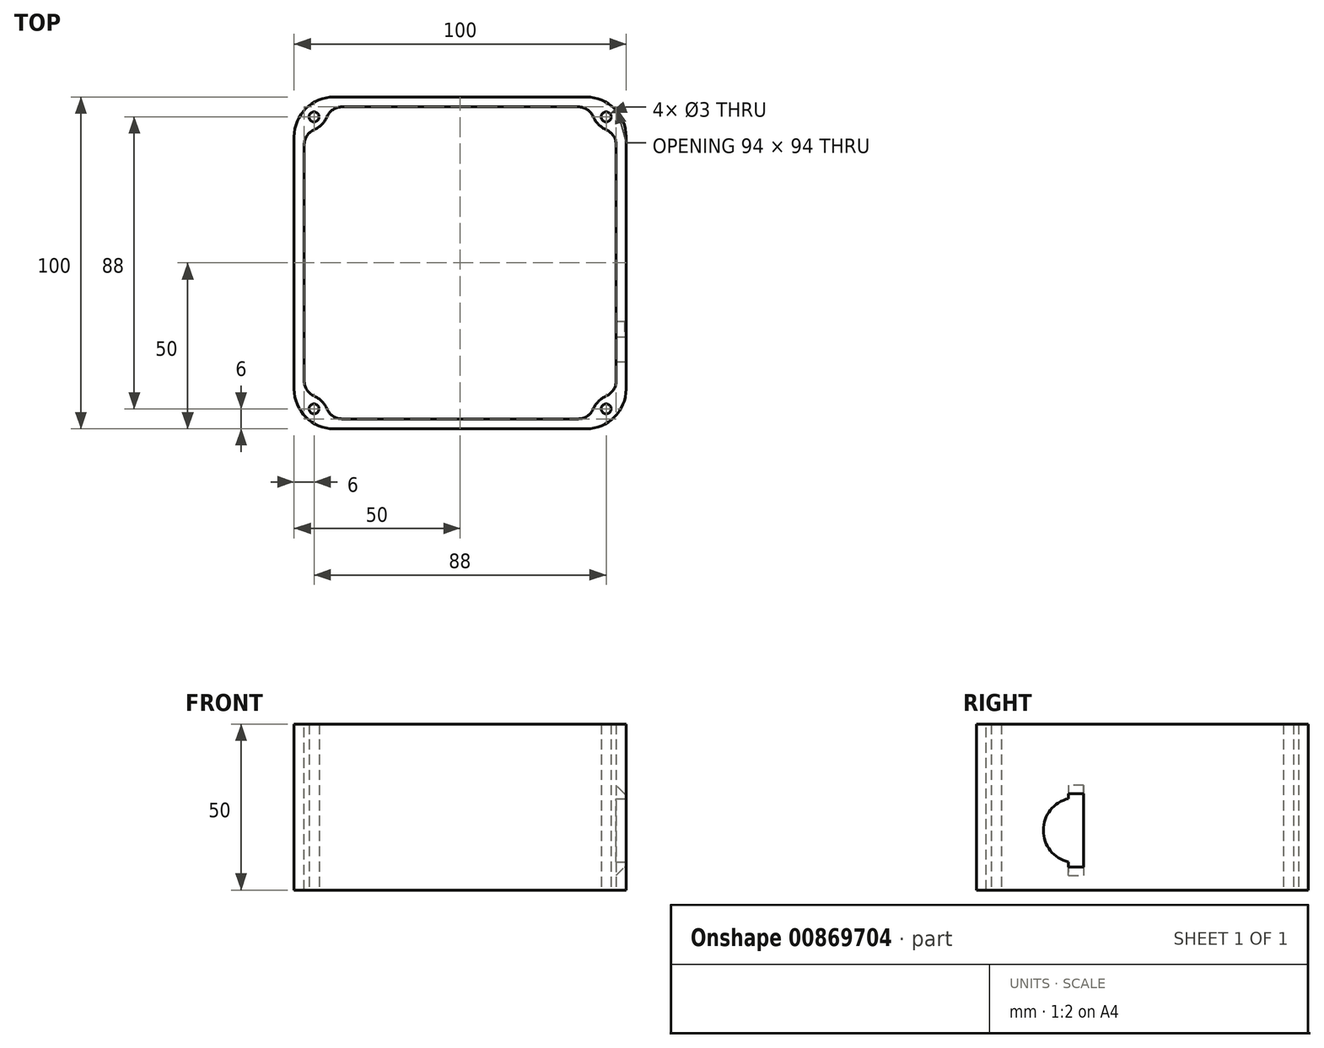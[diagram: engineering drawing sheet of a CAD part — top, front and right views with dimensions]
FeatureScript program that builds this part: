
annotation { "Feature Type Name" : "Feature", "Feature Type Description" : "" }
export const myFeature = defineFeature(function(context is Context, id is Id, definition is map)
    precondition{}
    {
        {
            var Q0;
            Q0=qCreatedBy(makeId("Top.planeOp"),FACE);
            var sketch = newSketch(context, id + "F0", { "sketchPlane" : qUnion([Q0])});
            skLineSegment(sketch, "E0.bottom", {"start": v(50, -50) * mm, "end": v(-50, -50) * mm});
            skLineSegment(sketch, "E0.top", {"start": v(50, 50) * mm, "end": v(-50, 50) * mm});
            skLineSegment(sketch, "E0.left", {"start": v(50, -50) * mm, "end": v(50, 50) * mm});
            skLineSegment(sketch, "E0.right", {"start": v(-50, -50) * mm, "end": v(-50, 50) * mm});
            skPoint(sketch, "E0.middle", {"position": v(0, 0) * mm});
            skLineSegment(sketch, "E1.bottom", {"start": v(47, -47) * mm, "end": v(-47, -47) * mm});
            skLineSegment(sketch, "E1.top", {"start": v(47, 47) * mm, "end": v(-47, 47) * mm});
            skLineSegment(sketch, "E1.left", {"start": v(47, -47) * mm, "end": v(47, 47) * mm});
            skLineSegment(sketch, "E1.right", {"start": v(-47, -47) * mm, "end": v(-47, 47) * mm});
            skLineSegment(sketch, "E2.bottom", {"start": v(-47, 47) * mm, "end": v(-44, 47) * mm, "construction": true});
            skLineSegment(sketch, "E2.top", {"start": v(-47, 44) * mm, "end": v(-44, 44) * mm, "construction": true});
            skLineSegment(sketch, "E2.left", {"start": v(-47, 47) * mm, "end": v(-47, 44) * mm, "construction": true});
            skLineSegment(sketch, "E2.right", {"start": v(-44, 47) * mm, "end": v(-44, 44) * mm, "construction": true});
            skLineSegment(sketch, "E3.bottom", {"start": v(47, 47) * mm, "end": v(44, 47) * mm, "construction": true});
            skLineSegment(sketch, "E3.top", {"start": v(47, 44) * mm, "end": v(44, 44) * mm, "construction": true});
            skLineSegment(sketch, "E3.left", {"start": v(47, 47) * mm, "end": v(47, 44) * mm, "construction": true});
            skLineSegment(sketch, "E3.right", {"start": v(44, 47) * mm, "end": v(44, 44) * mm, "construction": true});
            skLineSegment(sketch, "E4.bottom", {"start": v(47, -47) * mm, "end": v(44, -47) * mm, "construction": true});
            skLineSegment(sketch, "E4.top", {"start": v(47, -44) * mm, "end": v(44, -44) * mm, "construction": true});
            skLineSegment(sketch, "E4.left", {"start": v(47, -47) * mm, "end": v(47, -44) * mm, "construction": true});
            skLineSegment(sketch, "E4.right", {"start": v(44, -47) * mm, "end": v(44, -44) * mm, "construction": true});
            skLineSegment(sketch, "E5.bottom", {"start": v(-47, -47) * mm, "end": v(-44, -47) * mm, "construction": true});
            skLineSegment(sketch, "E5.top", {"start": v(-47, -44) * mm, "end": v(-44, -44) * mm, "construction": true});
            skLineSegment(sketch, "E5.left", {"start": v(-47, -47) * mm, "end": v(-47, -44) * mm, "construction": true});
            skLineSegment(sketch, "E5.right", {"start": v(-44, -47) * mm, "end": v(-44, -44) * mm, "construction": true});
            skCircle(sketch, "E6", {"center": v(-44, -44) * mm, "radius": 1.5 * mm});
            skCircle(sketch, "E7", {"center": v(-44, 44) * mm, "radius": 1.5 * mm});
            skCircle(sketch, "E8", {"center": v(44, 44) * mm, "radius": 1.5 * mm});
            skCircle(sketch, "E9", {"center": v(44, -44) * mm, "radius": 1.5 * mm});
            skCircle(sketch, "E10", {"center": v(-47, 47) * mm, "radius": 7.5 * mm});
            skCircle(sketch, "E11", {"center": v(47, 47) * mm, "radius": 7.5 * mm});
            skCircle(sketch, "E12", {"center": v(47, -47) * mm, "radius": 7.5 * mm});
            skCircle(sketch, "E13", {"center": v(-47, -47) * mm, "radius": 7.5 * mm});
            skSolve(sketch);
        }
        {
            var Q0;
            {var subQ0=sQuery(id+"F0.wireOp",EDGE,"E13");var subQ1=sQuery(id+"F0.wireOp",EDGE,"E0.right");var subQ2=makeQuery(id+"F0.imprint","INTERSECT",VERTEX,{"derivedFrom":[subQ1,subQ0]});Q0=makeQuery(id+"F0.imprint","IMPRINT",FACE,{"disambiguationData":[TD([[makeQuery(id+"F0.imprint","IMPRINT",EDGE,{"disambiguationData":[TD([[subQ2,-1.0]])],"derivedFrom":subQ1}),-1.0]])]});}
            var Q1;
            {var subQ5=sQuery(id+"F0.wireOp",EDGE,"E0.bottom");var subQ8=sQuery(id+"F0.wireOp",EDGE,"E0.right");var subQ9=makeQuery(id+"F0.imprint","INTERSECT",VERTEX,{"derivedFrom":[subQ5,subQ8]});Q1=makeQuery(id+"F0.imprint","IMPRINT",FACE,{"disambiguationData":[TD([[makeQuery(id+"F0.imprint","IMPRINT",EDGE,{"disambiguationData":[TD([[subQ9,1.0]])],"derivedFrom":subQ5}),-1.0]])]});}
            var Q2;
            Q2=makeQuery(id+"F0.imprint","IMPRINT",FACE,{"disambiguationData":[TD([[makeQuery(id+"F0.imprint","IMPRINT",EDGE,{"derivedFrom":sQuery(id+"F0.wireOp",EDGE,"E6")}),-1.0]])]});
            var Q3;
            {var subQ0=sQuery(id+"F0.wireOp",EDGE,"E12");var subQ1=sQuery(id+"F0.wireOp",EDGE,"E0.bottom");var subQ2=makeQuery(id+"F0.imprint","INTERSECT",VERTEX,{"derivedFrom":[subQ1,subQ0]});Q3=makeQuery(id+"F0.imprint","IMPRINT",FACE,{"disambiguationData":[TD([[makeQuery(id+"F0.imprint","IMPRINT",EDGE,{"disambiguationData":[TD([[subQ2,-1.0]])],"derivedFrom":subQ1}),-1.0]])]});}
            var Q4;
            {var subQ6=sQuery(id+"F0.wireOp",EDGE,"E0.left");var subQ7=sQuery(id+"F0.wireOp",EDGE,"E0.bottom");var subQ8=makeQuery(id+"F0.imprint","INTERSECT",VERTEX,{"derivedFrom":[subQ7,subQ6]});Q4=makeQuery(id+"F0.imprint","IMPRINT",FACE,{"disambiguationData":[TD([[makeQuery(id+"F0.imprint","IMPRINT",EDGE,{"disambiguationData":[TD([[subQ8,-1.0]])],"derivedFrom":subQ7}),-1.0]])]});}
            var Q5;
            Q5=makeQuery(id+"F0.imprint","IMPRINT",FACE,{"disambiguationData":[TD([[makeQuery(id+"F0.imprint","IMPRINT",EDGE,{"derivedFrom":sQuery(id+"F0.wireOp",EDGE,"E9")}),-1.0]])]});
            var Q6;
            {var subQ0=sQuery(id+"F0.wireOp",EDGE,"E12");var subQ1=sQuery(id+"F0.wireOp",EDGE,"E0.left");var subQ2=makeQuery(id+"F0.imprint","INTERSECT",VERTEX,{"derivedFrom":[subQ1,subQ0]});Q6=makeQuery(id+"F0.imprint","IMPRINT",FACE,{"disambiguationData":[TD([[makeQuery(id+"F0.imprint","IMPRINT",EDGE,{"disambiguationData":[TD([[subQ2,-1.0]])],"derivedFrom":subQ1}),1.0]])]});}
            var Q7;
            {var subQ6=sQuery(id+"F0.wireOp",EDGE,"E0.left");var subQ7=sQuery(id+"F0.wireOp",EDGE,"E0.top");var subQ8=makeQuery(id+"F0.imprint","INTERSECT",VERTEX,{"derivedFrom":[subQ7,subQ6]});Q7=makeQuery(id+"F0.imprint","IMPRINT",FACE,{"disambiguationData":[TD([[makeQuery(id+"F0.imprint","IMPRINT",EDGE,{"disambiguationData":[TD([[subQ8,-1.0]])],"derivedFrom":subQ7}),1.0]])]});}
            var Q8;
            Q8=makeQuery(id+"F0.imprint","IMPRINT",FACE,{"disambiguationData":[TD([[makeQuery(id+"F0.imprint","IMPRINT",EDGE,{"derivedFrom":sQuery(id+"F0.wireOp",EDGE,"E8")}),-1.0]])]});
            var Q9;
            {var subQ0=sQuery(id+"F0.wireOp",EDGE,"E11");var subQ1=sQuery(id+"F0.wireOp",EDGE,"E0.top");var subQ2=makeQuery(id+"F0.imprint","INTERSECT",VERTEX,{"derivedFrom":[subQ1,subQ0]});Q9=makeQuery(id+"F0.imprint","IMPRINT",FACE,{"disambiguationData":[TD([[makeQuery(id+"F0.imprint","IMPRINT",EDGE,{"disambiguationData":[TD([[subQ2,-1.0]])],"derivedFrom":subQ1}),1.0]])]});}
            var Q10;
            {var subQ6=sQuery(id+"F0.wireOp",EDGE,"E0.top");var subQ8=sQuery(id+"F0.wireOp",EDGE,"E0.right");var subQ9=makeQuery(id+"F0.imprint","INTERSECT",VERTEX,{"derivedFrom":[subQ6,subQ8]});Q10=makeQuery(id+"F0.imprint","IMPRINT",FACE,{"disambiguationData":[TD([[makeQuery(id+"F0.imprint","IMPRINT",EDGE,{"disambiguationData":[TD([[subQ9,1.0]])],"derivedFrom":subQ6}),1.0]])]});}
            var Q11;
            Q11=makeQuery(id+"F0.imprint","IMPRINT",FACE,{"disambiguationData":[TD([[makeQuery(id+"F0.imprint","IMPRINT",EDGE,{"derivedFrom":sQuery(id+"F0.wireOp",EDGE,"E7")}),-1.0]])]});
            extrude(context, id + "F1", {"entities" : qUnion([Q0, Q1, Q2, Q3, Q4, Q5, Q6, Q7, Q8, Q9, Q10, Q11]), "depth" : 50 * mm, "offsetDistance" : 25 * mm});
        }
        {
            var Q0;
            Q0=makeQuery(id+"F1.opExtrude","SWEPT_EDGE",EDGE,{"disambiguationData":[OSD([sQuery(id+"F0.wireOp",EDGE,"E0.top"),sQuery(id+"F0.wireOp",EDGE,"E0.right")])]});
            var Q1;
            Q1=makeQuery(id+"F1.opExtrude","SWEPT_EDGE",EDGE,{"disambiguationData":[OSD([sQuery(id+"F0.wireOp",EDGE,"E0.top"),sQuery(id+"F0.wireOp",EDGE,"E0.left")])]});
            var Q2;
            Q2=makeQuery(id+"F1.opExtrude","SWEPT_EDGE",EDGE,{"disambiguationData":[OSD([sQuery(id+"F0.wireOp",EDGE,"E0.bottom"),sQuery(id+"F0.wireOp",EDGE,"E0.left")])]});
            var Q3;
            Q3=makeQuery(id+"F1.opExtrude","SWEPT_EDGE",EDGE,{"disambiguationData":[OSD([sQuery(id+"F0.wireOp",EDGE,"E0.bottom"),sQuery(id+"F0.wireOp",EDGE,"E0.right")])]});
            fillet(context, id + "F2", {"entities" : qUnion([Q0, Q1, Q2, Q3]), "radius" : 12 * mm, "tangentPropagation" : true, "allowEdgeOverflow" : false});
        }
        {
            var Q0;
            Q0=makeQuery(id+"F1.opExtrude","SWEPT_EDGE",EDGE,{"disambiguationData":[OSD([sQuery(id+"F0.wireOp",EDGE,"E1.right"),sQuery(id+"F0.wireOp",EDGE,"E13")])]});
            var Q1;
            Q1=makeQuery(id+"F1.opExtrude","SWEPT_EDGE",EDGE,{"disambiguationData":[OSD([sQuery(id+"F0.wireOp",EDGE,"E1.bottom"),sQuery(id+"F0.wireOp",EDGE,"E13")])]});
            var Q2;
            Q2=makeQuery(id+"F1.opExtrude","SWEPT_EDGE",EDGE,{"disambiguationData":[OSD([sQuery(id+"F0.wireOp",EDGE,"E1.bottom"),sQuery(id+"F0.wireOp",EDGE,"E12")])]});
            var Q3;
            Q3=makeQuery(id+"F1.opExtrude","SWEPT_EDGE",EDGE,{"disambiguationData":[OSD([sQuery(id+"F0.wireOp",EDGE,"E1.left"),sQuery(id+"F0.wireOp",EDGE,"E12")])]});
            var Q4;
            Q4=makeQuery(id+"F1.opExtrude","SWEPT_EDGE",EDGE,{"disambiguationData":[OSD([sQuery(id+"F0.wireOp",EDGE,"E1.top"),sQuery(id+"F0.wireOp",EDGE,"E11")])]});
            var Q5;
            Q5=makeQuery(id+"F1.opExtrude","SWEPT_EDGE",EDGE,{"disambiguationData":[OSD([sQuery(id+"F0.wireOp",EDGE,"E1.left"),sQuery(id+"F0.wireOp",EDGE,"E11")])]});
            var Q6;
            Q6=makeQuery(id+"F1.opExtrude","SWEPT_EDGE",EDGE,{"disambiguationData":[OSD([sQuery(id+"F0.wireOp",EDGE,"E1.right"),sQuery(id+"F0.wireOp",EDGE,"E10")])]});
            var Q7;
            Q7=makeQuery(id+"F1.opExtrude","SWEPT_EDGE",EDGE,{"disambiguationData":[OSD([sQuery(id+"F0.wireOp",EDGE,"E1.top"),sQuery(id+"F0.wireOp",EDGE,"E10")])]});
            fillet(context, id + "F3", {"entities" : qUnion([Q0, Q1, Q2, Q3, Q4, Q5, Q6, Q7]), "radius" : 5 * mm, "tangentPropagation" : true, "allowEdgeOverflow" : false});
        }
        {
            var Q0;
            Q0=makeQuery(id+"F1.opExtrude","SWEPT_FACE",FACE,{"disambiguationData":[OSD([sQuery(id+"F0.wireOp",EDGE,"E0.left")])]});
            var sketch = newSketch(context, id + "F4", { "sketchPlane" : qUnion([Q0])});
            skCircle(sketch, "E14", {"center": v(-20, 18) * mm, "radius": 9.82 * mm});
            skLineSegment(sketch, "E15.bottom", {"start": v(-17.75, 6.95) * mm, "end": v(-22.25, 6.95) * mm});
            skLineSegment(sketch, "E15.top", {"start": v(-17.75, 29.05) * mm, "end": v(-22.25, 29.05) * mm});
            skLineSegment(sketch, "E15.left", {"start": v(-17.75, 6.95) * mm, "end": v(-17.75, 29.05) * mm});
            skLineSegment(sketch, "E15.right", {"start": v(-22.25, 6.95) * mm, "end": v(-22.25, 29.05) * mm});
            skLineSegment(sketch, "E16.bottom", {"start": v(-38, 0) * mm, "end": v(-20, 0) * mm, "construction": true});
            skLineSegment(sketch, "E16.top", {"start": v(-38, 18) * mm, "end": v(-20, 18) * mm, "construction": true});
            skLineSegment(sketch, "E16.left", {"start": v(-38, 0) * mm, "end": v(-38, 18) * mm, "construction": true});
            skLineSegment(sketch, "E16.right", {"start": v(-20, 0) * mm, "end": v(-20, 18) * mm, "construction": true});
            skSolve(sketch);
        }
        {
            var Q0;
            {var subQ0=sQuery(id+"F4.wireOp",EDGE,"E15.right");var subQ1=sQuery(id+"F4.wireOp",EDGE,"E14");var subQ2=makeQuery(id+"F4.imprint","INTERSECT",VERTEX,{"disambiguationData":[OD(0.0)],"derivedFrom":[subQ1,subQ0]});Q0=makeQuery(id+"F4.imprint","IMPRINT",FACE,{"disambiguationData":[TD([[makeQuery(id+"F4.imprint","IMPRINT",EDGE,{"disambiguationData":[TD([[subQ2,-1.0]])],"derivedFrom":subQ1}),1.0]])]});}
            var Q1;
            {var subQ0=sQuery(id+"F4.wireOp",EDGE,"E15.right");var subQ1=sQuery(id+"F4.wireOp",EDGE,"E14");var subQ2=makeQuery(id+"F4.imprint","INTERSECT",VERTEX,{"disambiguationData":[OD(0.0)],"derivedFrom":[subQ1,subQ0]});Q1=makeQuery(id+"F4.imprint","IMPRINT",FACE,{"disambiguationData":[TD([[makeQuery(id+"F4.imprint","IMPRINT",EDGE,{"disambiguationData":[TD([[subQ2,1.0]])],"derivedFrom":subQ1}),1.0]])]});}
            var Q2;
            {var subQ0=sQuery(id+"F4.wireOp",EDGE,"E15.left");var subQ1=sQuery(id+"F4.wireOp",EDGE,"E14");var subQ2=makeQuery(id+"F4.imprint","INTERSECT",VERTEX,{"disambiguationData":[OD(0.0)],"derivedFrom":[subQ1,subQ0]});Q2=makeQuery(id+"F4.imprint","IMPRINT",FACE,{"disambiguationData":[TD([[makeQuery(id+"F4.imprint","IMPRINT",EDGE,{"disambiguationData":[TD([[subQ2,1.0]])],"derivedFrom":subQ1}),1.0]])]});}
            var Q3;
            {var subQ5=sQuery(id+"F4.wireOp",EDGE,"E15.top");Q3=makeQuery(id+"F4.imprint","IMPRINT",FACE,{"disambiguationData":[TD([[makeQuery(id+"F4.imprint","IMPRINT",EDGE,{"derivedFrom":subQ5}),1.0]])]});}
            var Q4;
            {var subQ5=sQuery(id+"F4.wireOp",EDGE,"E15.bottom");Q4=makeQuery(id+"F4.imprint","IMPRINT",FACE,{"disambiguationData":[TD([[makeQuery(id+"F4.imprint","IMPRINT",EDGE,{"derivedFrom":subQ5}),-1.0]])]});}
            extrude(context, id + "F5", {"entities" : qUnion([Q0, Q1, Q2, Q3, Q4]), "operationType" : NewBodyOperationType.REMOVE, "oppositeDirection" : true, "depth" : 4 * mm, "offsetDistance" : 25 * mm});
        }
        {
            var Q0;
            Q0=makeQuery(id+"F5.boolean.opBoolean","INTERSECT",EDGE,{"derivedFrom":[makeQuery(id+"F1.opExtrude","SWEPT_FACE",FACE,{"disambiguationData":[OSD([sQuery(id+"F0.wireOp",EDGE,"E1.left")])]}),makeQuery(id+"F5.opExtrude","SWEPT_FACE",FACE,{"disambiguationData":[OSD([sQuery(id+"F4.wireOp",EDGE,"E15.top")])]})]});
            var Q1;
            Q1=makeQuery(id+"F5.boolean.opBoolean","INTERSECT",EDGE,{"derivedFrom":[makeQuery(id+"F1.opExtrude","SWEPT_FACE",FACE,{"disambiguationData":[OSD([sQuery(id+"F0.wireOp",EDGE,"E1.left")])]}),makeQuery(id+"F5.opExtrude","SWEPT_FACE",FACE,{"disambiguationData":[OSD([sQuery(id+"F4.wireOp",EDGE,"E15.bottom")])]})]});
            chamfer(context, id + "F6", {"entities" : qUnion([Q0, Q1]), "width" : 2.5 * mm, "tangentPropagation" : true});
        }
    });
